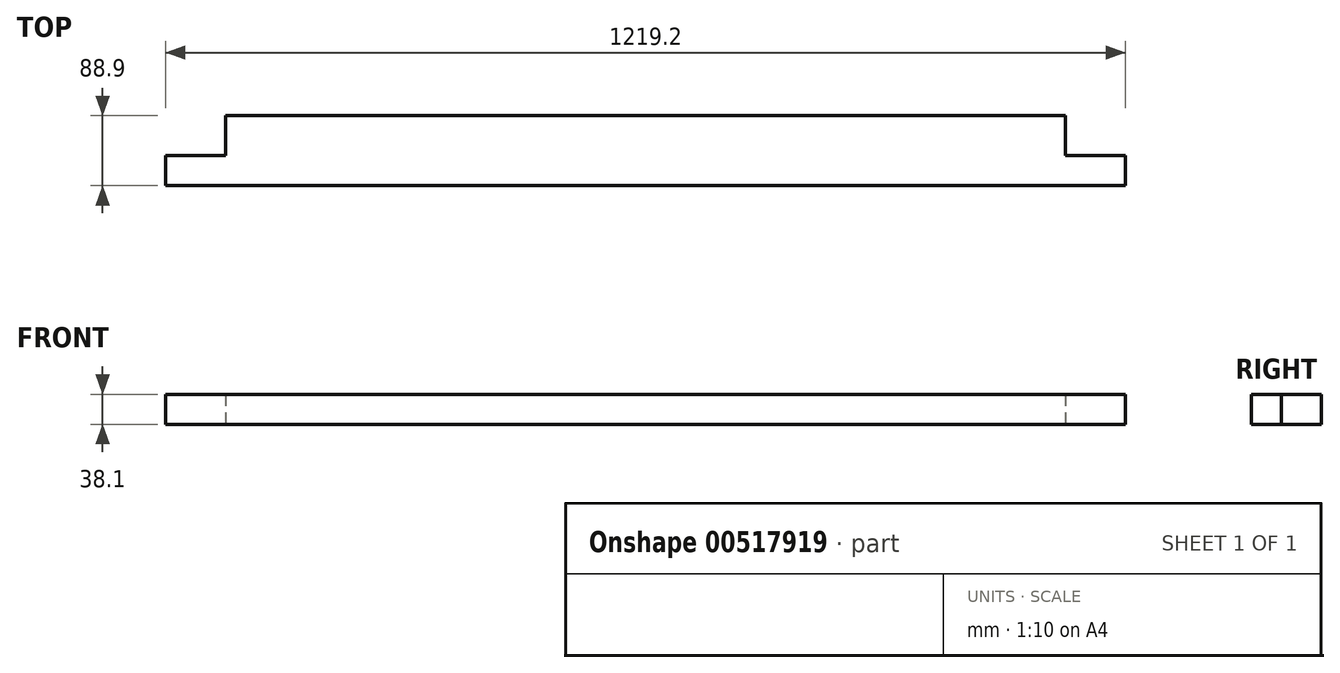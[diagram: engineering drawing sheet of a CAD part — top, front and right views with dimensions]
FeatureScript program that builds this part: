
annotation { "Feature Type Name" : "Feature", "Feature Type Description" : "" }
export const myFeature = defineFeature(function(context is Context, id is Id, definition is map)
    precondition{}
    {
        {
            var Q0;
            Q0=qCreatedBy(makeId("Top.planeOp"),FACE);
            var sketch = newSketch(context, id + "F0", { "sketchPlane" : qUnion([Q0])});
            skLineSegment(sketch, "E0.bottom", {"start": v(-533.4, 88.9) * mm, "end": v(533.4, 88.9) * mm});
            skLineSegment(sketch, "E0.left", {"start": v(-609.6, 38.1) * mm, "end": v(-609.6, 0) * mm});
            skLineSegment(sketch, "E0.right", {"start": v(609.6, 38.1) * mm, "end": v(609.6, 0) * mm});
            skLineSegment(sketch, "E1", {"start": v(-609.6, 0) * mm, "end": v(609.6, 0) * mm});
            skLineSegment(sketch, "E2.top", {"start": v(-609.6, 38.1) * mm, "end": v(-533.4, 38.1) * mm});
            skLineSegment(sketch, "E2.right", {"start": v(-533.4, 88.9) * mm, "end": v(-533.4, 38.1) * mm});
            skLineSegment(sketch, "E3.top", {"start": v(609.6, 38.1) * mm, "end": v(533.4, 38.1) * mm});
            skLineSegment(sketch, "E3.right", {"start": v(533.4, 88.9) * mm, "end": v(533.4, 38.1) * mm});
            skSolve(sketch);
        }
        {
            var Q0;
            Q0=makeQuery(id+"F0.imprint","IMPRINT",FACE,{"disambiguationData":[TD([[makeQuery(id+"F0.imprint","IMPRINT",EDGE,{"derivedFrom":sQuery(id+"F0.wireOp",EDGE,"E0.bottom")}),-1.0]])]});
            extrude(context, id + "F1", {"entities" : qUnion([Q0]), "endBound" : BoundingType.SYMMETRIC, "depth" : 38.1 * mm, "offsetDistance" : 25.4 * mm});
        }
    });
